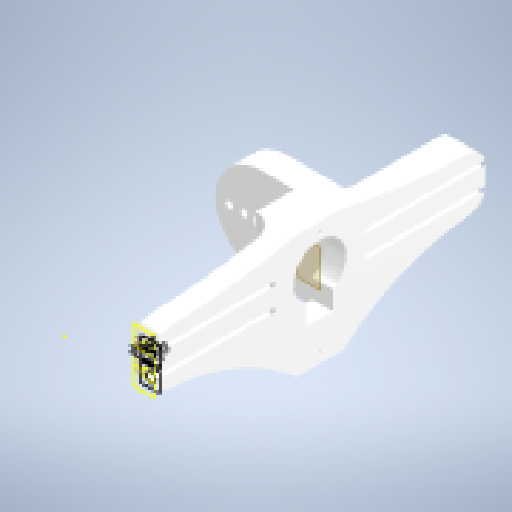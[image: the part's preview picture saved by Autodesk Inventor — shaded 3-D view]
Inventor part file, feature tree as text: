
AUTODESK INVENTOR PART (.ipt)
format: ipt  version: 2024 (Build 280153000, 153)  size: 788,992 bytes
history: native  units: in
note: dims shown in document units (in); Inventor stores cm internally (conversion verified against a paired STEP export)
features: other x6, projected_geometry x4, extrude x3, fillet x2, sketch x2, mirror x2, plane x1
ambient origin geometry x8: Origin, YZ Plane, XZ Plane, XY Plane, X Axis, Y Axis, Z Axis, Center Point
bodies: Solid1 (feature_tree)
feature tree (20):
  fillet  "Fillet9"  Radius=0.0886in
  other  "Axis1"
  other  "Axis2"
  other  "Plane1"
  other  "Plane2"
  other  "Plane3"
  other  "Plane4"
  sketch  "Sketch1"  dims[d5=0.0886in d6=0.0394in]
  extrude  "Extrusion1"  Depth=0.0394in
  extrude  "Extrusion2"  TaperAngle=45.0deg  [1 undecoded]
  plane  "Work Plane7"
  mirror  "Mirror1"
  extrude  "Extrusion3"  Depth=0.1969in
  mirror  "Mirror2"
  fillet  "Fillet1"  Radius=0.1969in
  projected_geometry  "Projected Loop1"
  projected_geometry  "Projected Loop2"
  projected_geometry  "Projected Loop6"
  projected_geometry  "Projected Loop7"
  sketch  "Sketch3"  dims[d7=0.0in d8=45.0deg d9=0.1969in d10=0.1969in d11=0.3937in d12=0.0in d13=0.0in d14=0.0in d18=0.0787in d19=-1.7283in d20=0.3937in d21=0.3937in d22=0.8912in d23=0.1635in d24=0.0in d25=0.0in d26=0.0039in]
note: 1 required parameter value undecoded (feature->parameter linkage not recoverable at this tier; creation-order binding heuristic only, values carry confidence <= 0.55)
